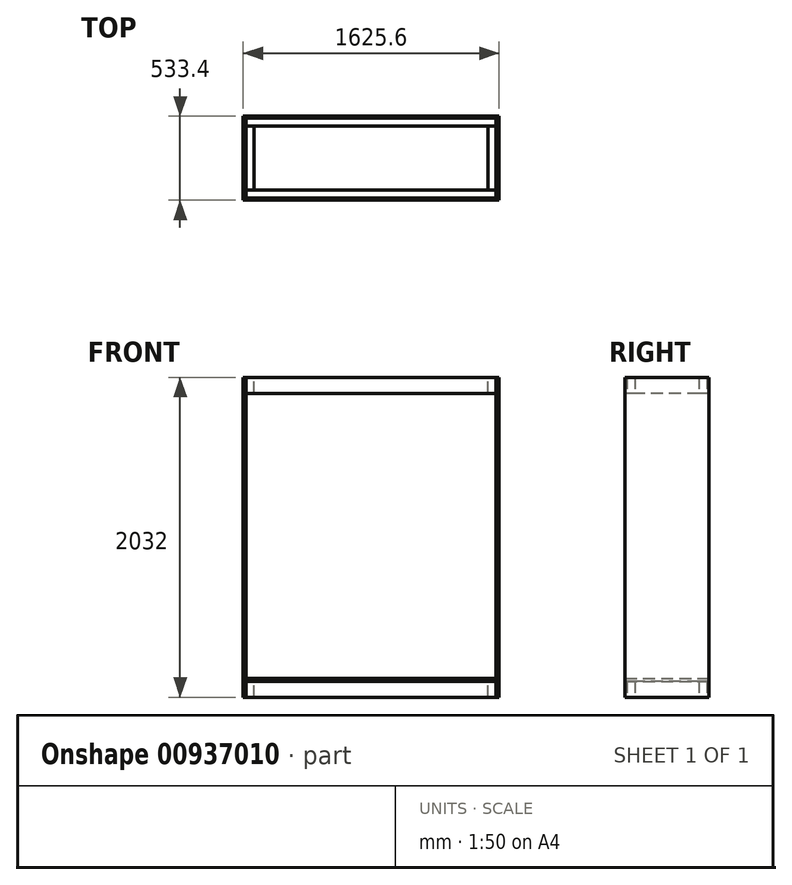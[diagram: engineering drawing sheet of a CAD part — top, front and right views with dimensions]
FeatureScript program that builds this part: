
annotation { "Feature Type Name" : "Feature", "Feature Type Description" : "" }
export const myFeature = defineFeature(function(context is Context, id is Id, definition is map)
    precondition{}
    {
        {
            var Q0;
            Q0=qCreatedBy(makeId("Front.planeOp"),FACE);
            var sketch = newSketch(context, id + "F0", { "sketchPlane" : qUnion([Q0])});
            skLineSegment(sketch, "E0", {"start": v(-793.75, 101.6) * mm, "end": v(793.75, 101.6) * mm});
            skLineSegment(sketch, "E1.0", {"start": v(-793.75, 1930.4) * mm, "end": v(793.75, 1930.4) * mm});
            skLineSegment(sketch, "E2.0", {"start": v(-812.8, 0) * mm, "end": v(812.8, 0) * mm});
            skLineSegment(sketch, "E3.0", {"start": v(-812.8, 2032) * mm, "end": v(812.8, 2032) * mm});
            skLineSegment(sketch, "E4", {"start": v(-812.8, 2032) * mm, "end": v(-812.8, 0) * mm});
            skLineSegment(sketch, "E5", {"start": v(812.8, 2032) * mm, "end": v(812.8, 0) * mm});
            skLineSegment(sketch, "E6.0", {"start": v(-793.75, 2032) * mm, "end": v(-793.75, 0) * mm});
            skLineSegment(sketch, "E7.0", {"start": v(793.75, 2032) * mm, "end": v(793.75, 0) * mm});
            skSolve(sketch);
        }
        {
            var Q0;
            {var subQ0=sQuery(id+"F0.wireOp",EDGE,"E1.0");Q0=makeQuery(id+"F0.imprint","IMPRINT",FACE,{"disambiguationData":[TD([[makeQuery(id+"F0.imprint","IMPRINT",EDGE,{"derivedFrom":subQ0}),1.0]])]});}
            extrude(context, id + "F1", {"entities" : qUnion([Q0]), "oppositeDirection" : true, "depth" : 50.8 * mm, "offsetDistance" : 25.4 * mm});
        }
        {
            var Q0;
            {var subQ0=sQuery(id+"F0.wireOp",EDGE,"E0");Q0=makeQuery(id+"F0.imprint","IMPRINT",FACE,{"disambiguationData":[TD([[makeQuery(id+"F0.imprint","IMPRINT",EDGE,{"derivedFrom":subQ0}),-1.0]])]});}
            extrude(context, id + "F2", {"entities" : qUnion([Q0]), "oppositeDirection" : true, "depth" : 50.8 * mm, "offsetDistance" : 25.4 * mm});
        }
        {
            var Q0;
            Q0=makeQuery(id+"F1.opExtrude","SWEPT_FACE",FACE,{"disambiguationData":[OSD([sQuery(id+"F0.wireOp",EDGE,"E7.0")])]});
            var sketch = newSketch(context, id + "F3", { "sketchPlane" : qUnion([Q0])});
            skLineSegment(sketch, "E8", {"start": v(0, 2032) * mm, "end": v(533.4, 2032) * mm});
            skLineSegment(sketch, "E9", {"start": v(533.4, 2032) * mm, "end": v(533.4, 0) * mm});
            skLineSegment(sketch, "E10", {"start": v(533.4, 0) * mm, "end": v(0, 0) * mm});
            skLineSegment(sketch, "E11", {"start": v(0, 0) * mm, "end": v(0, 2032) * mm});
            skSolve(sketch);
        }
        {
            var Q0;
            {var subQ1=sQuery(id+"F3.wireOp",EDGE,"E9");Q0=makeQuery(id+"F3.imprint","IMPRINT",FACE,{"disambiguationData":[TD([[makeQuery(id+"F3.imprint","IMPRINT",EDGE,{"derivedFrom":subQ1}),-1.0]])]});}
            var Q1;
            {var subQ3=sQuery(id+"F0.wireOp",EDGE,"E7.0");var subQ4=makeQuery(id+"F1.opExtrude","CAP_EDGE",EDGE,{"disambiguationData":[OSD([subQ3])],"isStart":false});Q1=makeQuery(id+"F3.imprint","IMPRINT",FACE,{"disambiguationData":[TD([[makeQuery(id+"F3.imprint","IMPRINT",EDGE,{"derivedFrom":subQ4}),-1.0]])]});}
            extrude(context, id + "F4", {"entities" : qUnion([Q0, Q1]), "depth" : 19.05 * mm, "offsetDistance" : 25.4 * mm});
        }
        {
            var Q0;
            Q0=makeQuery(id+"F1.opExtrude","SWEPT_BODY",BODY,{"disambiguationData":[OSD([sQuery(id+"F0.wireOp",EDGE,"E1.0"),sQuery(id+"F0.wireOp",EDGE,"E3.0"),sQuery(id+"F0.wireOp",EDGE,"E6.0"),sQuery(id+"F0.wireOp",EDGE,"E7.0")])]});
            var Q1;
            Q1=makeQuery(id+"F2.opExtrude","SWEPT_BODY",BODY,{"disambiguationData":[OSD([sQuery(id+"F0.wireOp",EDGE,"E0"),sQuery(id+"F0.wireOp",EDGE,"E2.0"),sQuery(id+"F0.wireOp",EDGE,"E6.0"),sQuery(id+"F0.wireOp",EDGE,"E7.0")])]});
            transform(context, id + "F5", {"entities" : qUnion([Q0, Q1]), "transformType" : TransformType.COPY});
        }
        {
            var Q0;
            Q0=makeQuery(id+"F5.opPattern","COPY",BODY,{"derivedFrom":makeQuery(id+"F2.opExtrude","SWEPT_BODY",BODY,{"disambiguationData":[OSD([sQuery(id+"F0.wireOp",EDGE,"E0"),sQuery(id+"F0.wireOp",EDGE,"E2.0"),sQuery(id+"F0.wireOp",EDGE,"E6.0"),sQuery(id+"F0.wireOp",EDGE,"E7.0")])]}),"instanceName":"1"});
            var Q1;
            Q1=makeQuery(id+"F5.opPattern","COPY",BODY,{"derivedFrom":makeQuery(id+"F1.opExtrude","SWEPT_BODY",BODY,{"disambiguationData":[OSD([sQuery(id+"F0.wireOp",EDGE,"E1.0"),sQuery(id+"F0.wireOp",EDGE,"E3.0"),sQuery(id+"F0.wireOp",EDGE,"E6.0"),sQuery(id+"F0.wireOp",EDGE,"E7.0")])]}),"instanceName":"1"});
            transform(context, id + "F6", {"entities" : qUnion([Q0, Q1]), "transformType" : TransformType.TRANSLATION_3D, "dx" : 0 * mm, "dy" : 482.6 * mm, "dz" : 0 * mm, "makeCopy" : false});
        }
        {
            var Q0;
            Q0=makeQuery(id+"F4.opExtrude","SWEPT_BODY",BODY,{"disambiguationData":[OSD([sQuery(id+"F3.wireOp",EDGE,"E8"),sQuery(id+"F3.wireOp",EDGE,"E9"),sQuery(id+"F3.wireOp",EDGE,"E10"),sQuery(id+"F3.wireOp",EDGE,"E11")])]});
            transform(context, id + "F7", {"entities" : qUnion([Q0]), "transformType" : TransformType.COPY});
        }
        {
            var Q0;
            Q0=makeQuery(id+"F7.opPattern","COPY",BODY,{"derivedFrom":makeQuery(id+"F4.opExtrude","SWEPT_BODY",BODY,{"disambiguationData":[OSD([sQuery(id+"F3.wireOp",EDGE,"E8"),sQuery(id+"F3.wireOp",EDGE,"E9"),sQuery(id+"F3.wireOp",EDGE,"E10"),sQuery(id+"F3.wireOp",EDGE,"E11")])]}),"instanceName":"1"});
            transform(context, id + "F8", {"entities" : qUnion([Q0]), "transformType" : TransformType.TRANSLATION_3D, "dx" : -1606.55 * mm, "dy" : 0 * mm, "dz" : 0 * mm, "makeCopy" : false});
        }
        {
            var Q0;
            Q0=makeQuery(id+"F5.opPattern","COPY",BODY,{"derivedFrom":makeQuery(id+"F1.opExtrude","SWEPT_BODY",BODY,{"disambiguationData":[OSD([sQuery(id+"F0.wireOp",EDGE,"E1.0"),sQuery(id+"F0.wireOp",EDGE,"E3.0"),sQuery(id+"F0.wireOp",EDGE,"E6.0"),sQuery(id+"F0.wireOp",EDGE,"E7.0")])]}),"instanceName":"1"});
            var Q1;
            Q1=makeQuery(id+"F5.opPattern","COPY",BODY,{"derivedFrom":makeQuery(id+"F2.opExtrude","SWEPT_BODY",BODY,{"disambiguationData":[OSD([sQuery(id+"F0.wireOp",EDGE,"E0"),sQuery(id+"F0.wireOp",EDGE,"E2.0"),sQuery(id+"F0.wireOp",EDGE,"E6.0"),sQuery(id+"F0.wireOp",EDGE,"E7.0")])]}),"instanceName":"1"});
            transform(context, id + "F9", {"entities" : qUnion([Q0, Q1]), "transformType" : TransformType.TRANSLATION_3D, "dx" : 0 * mm, "dy" : -12.7 * mm, "dz" : 0 * mm, "makeCopy" : false});
        }
        {
            var Q0;
            Q0=makeQuery(id+"F1.opExtrude","SWEPT_BODY",BODY,{"disambiguationData":[OSD([sQuery(id+"F0.wireOp",EDGE,"E1.0"),sQuery(id+"F0.wireOp",EDGE,"E3.0"),sQuery(id+"F0.wireOp",EDGE,"E6.0"),sQuery(id+"F0.wireOp",EDGE,"E7.0")])]});
            var Q1;
            Q1=makeQuery(id+"F2.opExtrude","SWEPT_BODY",BODY,{"disambiguationData":[OSD([sQuery(id+"F0.wireOp",EDGE,"E0"),sQuery(id+"F0.wireOp",EDGE,"E2.0"),sQuery(id+"F0.wireOp",EDGE,"E6.0"),sQuery(id+"F0.wireOp",EDGE,"E7.0")])]});
            transform(context, id + "F10", {"entities" : qUnion([Q0, Q1]), "transformType" : TransformType.TRANSLATION_3D, "dx" : 0 * mm, "dy" : 12.7 * mm, "dz" : 0 * mm, "makeCopy" : false});
        }
        {
            var Q0;
            Q0=makeQuery(id+"F5.opPattern","COPY",FACE,{"derivedFrom":makeQuery(id+"F1.opExtrude","SWEPT_FACE",FACE,{"disambiguationData":[OSD([sQuery(id+"F0.wireOp",EDGE,"E3.0")])]}),"instanceName":"1"});
            var sketch = newSketch(context, id + "F11", { "sketchPlane" : qUnion([Q0])});
            skLineSegment(sketch, "E12", {"start": v(-793.75, 469.9) * mm, "end": v(-793.75, 63.5) * mm});
            skLineSegment(sketch, "E13", {"start": v(-793.75, 63.5) * mm, "end": v(-742.95, 63.5) * mm});
            skLineSegment(sketch, "E14", {"start": v(-742.95, 63.5) * mm, "end": v(-742.95, 469.9) * mm});
            skLineSegment(sketch, "E15", {"start": v(-742.95, 469.9) * mm, "end": v(-793.75, 469.9) * mm});
            skSolve(sketch);
        }
        {
            var Q0;
            Q0=makeQuery(id+"F11.imprint","IMPRINT",FACE,{"disambiguationData":[TD([[makeQuery(id+"F11.imprint","IMPRINT",EDGE,{"derivedFrom":sQuery(id+"F11.wireOp",EDGE,"E12")}),1.0]])]});
            extrude(context, id + "F12", {"entities" : qUnion([Q0]), "oppositeDirection" : true, "depth" : 101.6 * mm, "offsetDistance" : 25.4 * mm});
        }
        {
            var Q0;
            Q0=makeQuery(id+"F12.opExtrude","SWEPT_BODY",BODY,{"disambiguationData":[OSD([sQuery(id+"F11.wireOp",EDGE,"E12"),sQuery(id+"F11.wireOp",EDGE,"E13"),sQuery(id+"F11.wireOp",EDGE,"E14"),sQuery(id+"F11.wireOp",EDGE,"E15")])]});
            transform(context, id + "F13", {"entities" : qUnion([Q0]), "transformType" : TransformType.COPY});
        }
        {
            var Q0;
            Q0=makeQuery(id+"F13.opPattern","COPY",BODY,{"derivedFrom":makeQuery(id+"F12.opExtrude","SWEPT_BODY",BODY,{"disambiguationData":[OSD([sQuery(id+"F11.wireOp",EDGE,"E12"),sQuery(id+"F11.wireOp",EDGE,"E13"),sQuery(id+"F11.wireOp",EDGE,"E14"),sQuery(id+"F11.wireOp",EDGE,"E15")])]}),"instanceName":"1"});
            transform(context, id + "F14", {"entities" : qUnion([Q0]), "transformType" : TransformType.TRANSLATION_3D, "dx" : 1536.7 * mm, "dy" : 0 * mm, "dz" : 0 * mm, "makeCopy" : false});
        }
        {
            var Q0;
            Q0=makeQuery(id+"F12.opExtrude","SWEPT_BODY",BODY,{"disambiguationData":[OSD([sQuery(id+"F11.wireOp",EDGE,"E12"),sQuery(id+"F11.wireOp",EDGE,"E13"),sQuery(id+"F11.wireOp",EDGE,"E14"),sQuery(id+"F11.wireOp",EDGE,"E15")])]});
            var Q1;
            Q1=makeQuery(id+"F13.opPattern","COPY",BODY,{"derivedFrom":makeQuery(id+"F12.opExtrude","SWEPT_BODY",BODY,{"disambiguationData":[OSD([sQuery(id+"F11.wireOp",EDGE,"E12"),sQuery(id+"F11.wireOp",EDGE,"E13"),sQuery(id+"F11.wireOp",EDGE,"E14"),sQuery(id+"F11.wireOp",EDGE,"E15")])]}),"instanceName":"1"});
            transform(context, id + "F15", {"entities" : qUnion([Q0, Q1]), "transformType" : TransformType.COPY});
        }
        {
            var Q0;
            Q0=makeQuery(id+"F15.opPattern","COPY",BODY,{"derivedFrom":makeQuery(id+"F12.opExtrude","SWEPT_BODY",BODY,{"disambiguationData":[OSD([sQuery(id+"F11.wireOp",EDGE,"E12"),sQuery(id+"F11.wireOp",EDGE,"E13"),sQuery(id+"F11.wireOp",EDGE,"E14"),sQuery(id+"F11.wireOp",EDGE,"E15")])]}),"instanceName":"1"});
            var Q1;
            Q1=makeQuery(id+"F15.opPattern","COPY",BODY,{"derivedFrom":makeQuery(id+"F13.opPattern","COPY",BODY,{"derivedFrom":makeQuery(id+"F12.opExtrude","SWEPT_BODY",BODY,{"disambiguationData":[OSD([sQuery(id+"F11.wireOp",EDGE,"E12"),sQuery(id+"F11.wireOp",EDGE,"E13"),sQuery(id+"F11.wireOp",EDGE,"E14"),sQuery(id+"F11.wireOp",EDGE,"E15")])]}),"instanceName":"1"}),"instanceName":"1"});
            transform(context, id + "F16", {"entities" : qUnion([Q0, Q1]), "transformType" : TransformType.TRANSLATION_3D, "dx" : 0 * mm, "dy" : 0 * mm, "dz" : -1930.4 * mm, "makeCopy" : false});
        }
        {
            var Q0;
            Q0=makeQuery(id+"F7.opPattern","COPY",FACE,{"derivedFrom":makeQuery(id+"F4.opExtrude","SWEPT_FACE",FACE,{"disambiguationData":[OSD([sQuery(id+"F3.wireOp",EDGE,"E8")])]}),"instanceName":"1"});
            var sketch = newSketch(context, id + "F17", { "sketchPlane" : qUnion([Q0])});
            skLineSegment(sketch, "E16.bottom", {"start": v(-793.75, 533.4) * mm, "end": v(793.75, 533.4) * mm});
            skLineSegment(sketch, "E16.top", {"start": v(-793.75, 0) * mm, "end": v(793.75, 0) * mm});
            skLineSegment(sketch, "E16.left", {"start": v(-793.75, 533.4) * mm, "end": v(-793.75, 0) * mm});
            skLineSegment(sketch, "E16.right", {"start": v(793.75, 533.4) * mm, "end": v(793.75, 0) * mm});
            skSolve(sketch);
        }
        {
            var Q0;
            Q0=makeQuery(id+"F17.imprint","IMPRINT",FACE,{"disambiguationData":[TD([[makeQuery(id+"F17.imprint","IMPRINT",EDGE,{"derivedFrom":sQuery(id+"F17.wireOp",EDGE,"E16.bottom")}),-1.0]])]});
            extrude(context, id + "F18", {"entities" : qUnion([Q0]), "depth" : 19.05 * mm, "offsetDistance" : 25.4 * mm});
        }
        {
            var Q0;
            Q0=makeQuery(id+"F18.opExtrude","SWEPT_BODY",BODY,{"disambiguationData":[OSD([sQuery(id+"F17.wireOp",EDGE,"E16.bottom"),sQuery(id+"F17.wireOp",EDGE,"E16.top"),sQuery(id+"F17.wireOp",EDGE,"E16.left"),sQuery(id+"F17.wireOp",EDGE,"E16.right")])]});
            transform(context, id + "F19", {"entities" : qUnion([Q0]), "transformType" : TransformType.TRANSLATION_3D, "dx" : 0 * mm, "dy" : 0 * mm, "dz" : -1930.4 * mm, "makeCopy" : false});
        }
    });
